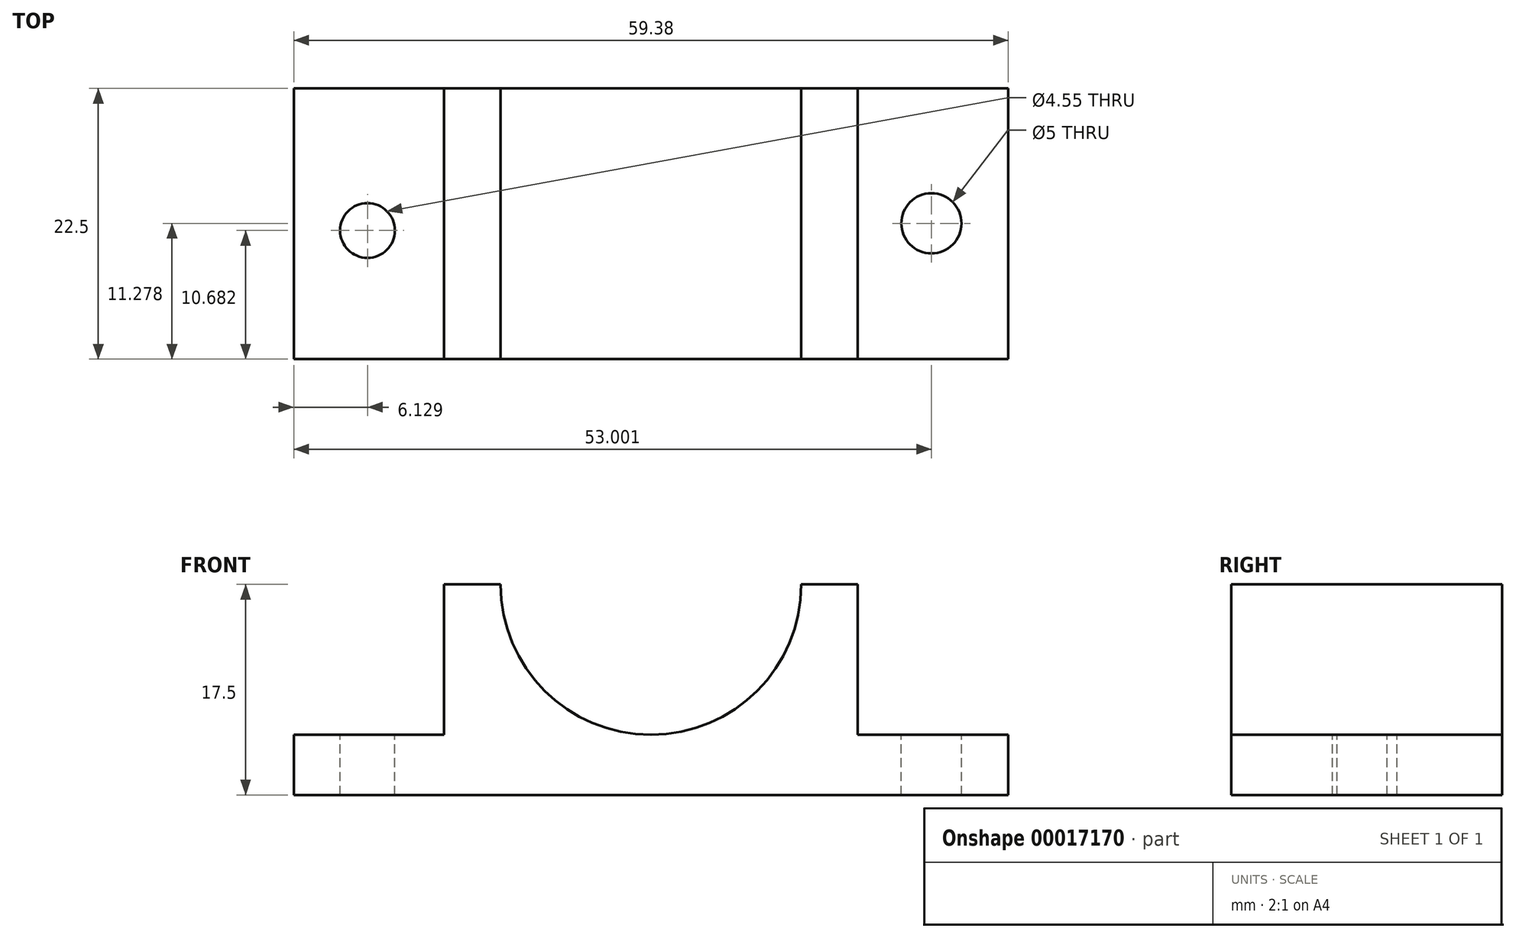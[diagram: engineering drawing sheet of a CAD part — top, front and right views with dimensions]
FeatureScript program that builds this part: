
annotation { "Feature Type Name" : "Feature", "Feature Type Description" : "" }
export const myFeature = defineFeature(function(context is Context, id is Id, definition is map)
    precondition{}
    {
        {
            var Q0;
            Q0=qCreatedBy(makeId("Front.planeOp"),FACE);
            var sketch = newSketch(context, id + "F0", { "sketchPlane" : qUnion([Q0])});
            skPoint(sketch, "E0.center.orphan", {"position": v(7.34, 21.12) * mm});
            skPoint(sketch, "E1.left.end.orphan", {"position": v(1.37, 21.12) * mm});
            skPoint(sketch, "E1.right.end.orphan", {"position": v(13.31, 21.12) * mm});
            skLineSegment(sketch, "E2.bottom", {"start": v(-25.99, -8.36) * mm, "end": v(33.39, -8.36) * mm});
            skLineSegment(sketch, "E2.top", {"start": v(-13.49, 9.14) * mm, "end": v(-8.8, 9.14) * mm});
            skLineSegment(sketch, "E2.left", {"start": v(-25.99, -8.36) * mm, "end": v(-25.99, -3.36) * mm});
            skLineSegment(sketch, "E2.right", {"start": v(33.39, -8.36) * mm, "end": v(33.39, -3.36) * mm});
            skLineSegment(sketch, "E3", {"start": v(-25.99, -3.36) * mm, "end": v(-13.49, -3.36) * mm});
            skLineSegment(sketch, "E4", {"start": v(-13.49, 9.14) * mm, "end": v(-13.49, -3.36) * mm});
            skLineSegment(sketch, "E5", {"start": v(33.39, -3.36) * mm, "end": v(20.89, -3.36) * mm});
            skLineSegment(sketch, "E6", {"start": v(20.89, -3.36) * mm, "end": v(20.89, 9.14) * mm});
            skArc(sketch, "E7", {"start": v(-8.8, 9.14) * mm, "mid": v(3.7, -3.36) * mm, "end": v(16.2, 9.14) * mm});
            skLineSegment(sketch, "E8.trimOffspring", {"start": v(16.2, 9.14) * mm, "end": v(20.89, 9.14) * mm});
            skSolve(sketch);
        }
        {
            var Q0;
            Q0 = qSketchRegion(id + "F0", true);
            extrude(context, id + "F1", {"entities" : qUnion([Q0]), "depth" : 22.5 * mm});
        }
        {
            var Q0;
            Q0=qCreatedBy(makeId("Top.planeOp"),FACE);
            var sketch = newSketch(context, id + "F2", { "sketchPlane" : qUnion([Q0])});
            skPoint(sketch, "E9.start.orphan", {"position": v(-11.26, 0) * mm});
            skPoint(sketch, "E10.trimOffspring.end.orphan", {"position": v(-28.46, -23.63) * mm});
            skPoint(sketch, "E11.orphan", {"position": v(11.7, 0) * mm});
            skPoint(sketch, "E12.start.orphan", {"position": v(42.32, -22.44) * mm});
            skCircle(sketch, "E13", {"center": v(27.01, -11.22) * mm, "radius": 2.5 * mm});
            skPoint(sketch, "E14.center.orphan", {"position": v(-19.86, -11.82) * mm});
            skPoint(sketch, "E15.start.orphan", {"position": v(-14.6, 0) * mm});
            skCircle(sketch, "E16", {"center": v(-19.86, -11.82) * mm, "radius": 2.28 * mm});
            skPoint(sketch, "E17.orphan", {"position": v(15.22, 0) * mm});
            skSolve(sketch);
        }
        {
            var Q0;
            Q0 = qSketchRegion(id + "F2", true);
            extrude(context, id + "F3", {"entities" : qUnion([Q0]), "operationType" : NewBodyOperationType.REMOVE, "oppositeDirection" : true, "depth" : 25 * mm});
        }
    });
